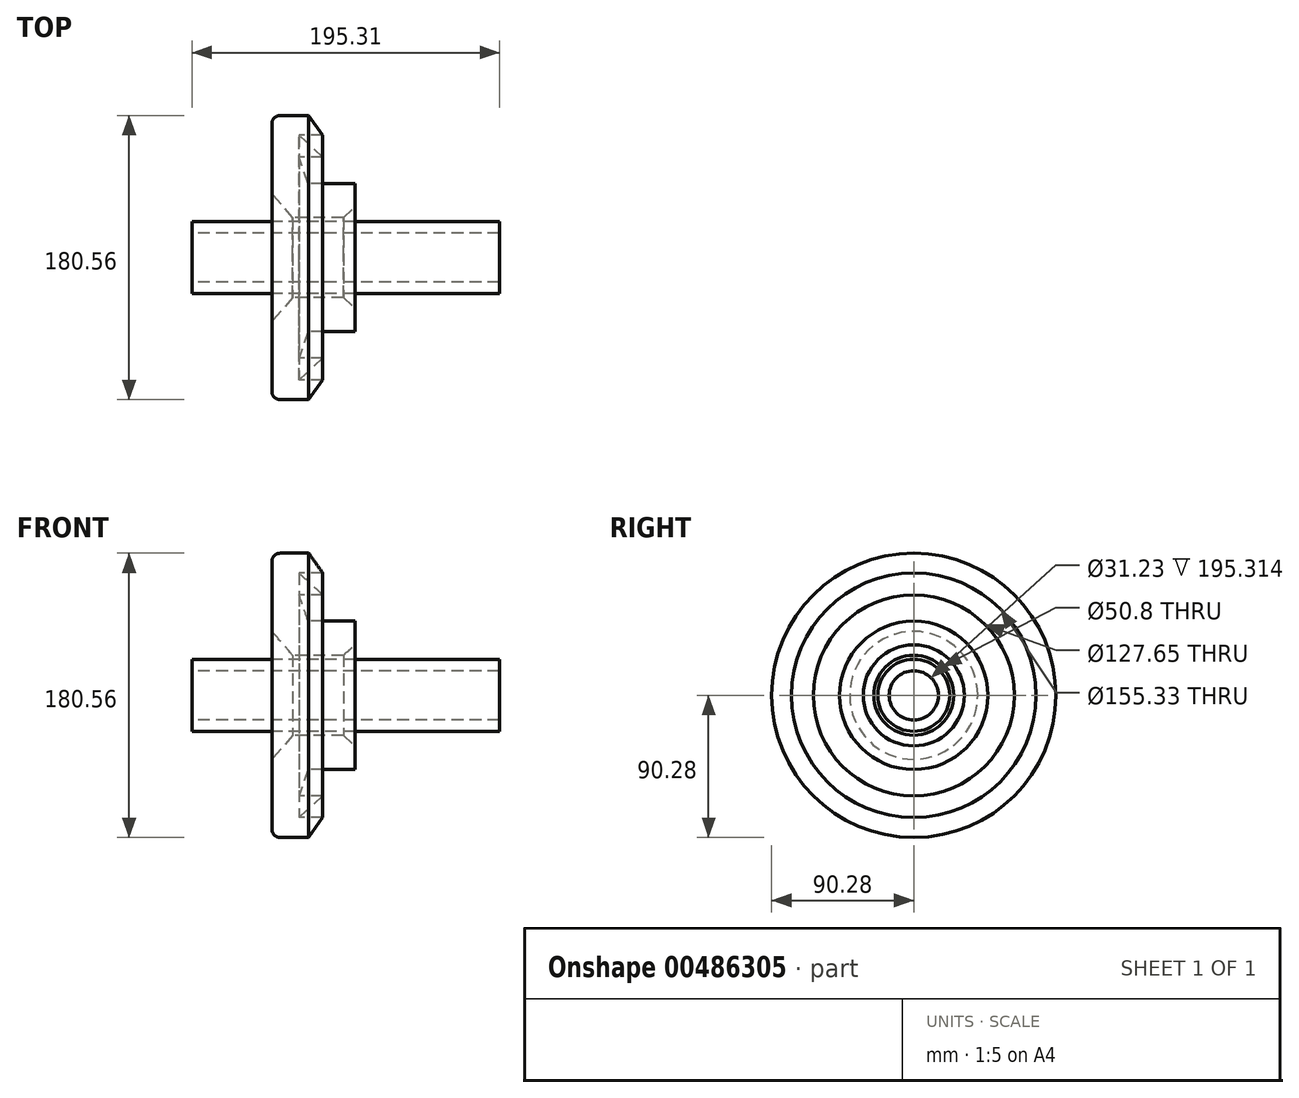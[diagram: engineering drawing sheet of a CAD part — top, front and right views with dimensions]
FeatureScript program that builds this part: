
annotation { "Feature Type Name" : "Feature", "Feature Type Description" : "" }
export const myFeature = defineFeature(function(context is Context, id is Id, definition is map)
    precondition{}
    {
        {
            var Q0;
            Q0=qCreatedBy(makeId("Front.planeOp"),FACE);
            var sketch = newSketch(context, id + "F0", { "sketchPlane" : qUnion([Q0])});
            skLineSegment(sketch, "E0", {"start": v(13.13, 0) * mm, "end": v(0, 15.22) * mm});
            skLineSegment(sketch, "E1", {"start": v(0, 15.22) * mm, "end": v(0, 64.88) * mm});
            skLineSegment(sketch, "E2", {"start": v(0, 64.88) * mm, "end": v(23.3, 64.88) * mm});
            skLineSegment(sketch, "E3", {"start": v(23.3, 64.88) * mm, "end": v(32.26, 52.26) * mm});
            skLineSegment(sketch, "E4", {"start": v(32.26, 52.26) * mm, "end": v(17.2, 52.26) * mm});
            skLineSegment(sketch, "E5", {"start": v(17.2, 52.26) * mm, "end": v(32.26, 38.42) * mm});
            skLineSegment(sketch, "E6", {"start": v(32.26, 38.42) * mm, "end": v(17.2, 38.42) * mm});
            skLineSegment(sketch, "E7", {"start": v(17.2, 38.42) * mm, "end": v(22.9, 21.74) * mm});
            skLineSegment(sketch, "E8", {"start": v(22.9, 21.74) * mm, "end": v(52.62, 21.74) * mm});
            skLineSegment(sketch, "E9", {"start": v(52.62, 21.74) * mm, "end": v(52.62, 6.68) * mm});
            skLineSegment(sketch, "E10", {"start": v(52.62, 6.68) * mm, "end": v(45.29, 0) * mm});
            skLineSegment(sketch, "E11", {"start": v(45.29, 0) * mm, "end": v(13.13, 0) * mm});
            skLineSegment(sketch, "E12", {"start": v(-104.09, -25.4) * mm, "end": v(175.13, -25.4) * mm});
            skSolve(sketch);
        }
        {
            var Q0;
            Q0=makeQuery(id+"F0.imprint","IMPRINT",FACE,{"disambiguationData":[TD([[makeQuery(id+"F0.imprint","IMPRINT",EDGE,{"derivedFrom":sQuery(id+"F0.wireOp",EDGE,"E0")}),-1.0]])]});
            var Q1;
            Q1=sQuery(id+"F0.wireOp",EDGE,"E12");
            revolve(context, id + "F1", {"surfaceOperationType" : NewSurfaceOperationType.NEW, "entities" : qUnion([Q0]), "axis" : qUnion([Q1]), "revolveType" : RevolveType.FULL});
        }
        {
            var Q0;
            Q0=qCreatedBy(makeId("Front.planeOp"),FACE);
            var sketch = newSketch(context, id + "F2", { "sketchPlane" : qUnion([Q0])});
            skLineSegment(sketch, "E13.bottom", {"start": v(-50.8, -2.54) * mm, "end": v(144.51, -2.54) * mm});
            skLineSegment(sketch, "E13.top", {"start": v(-50.8, -9.79) * mm, "end": v(144.51, -9.79) * mm});
            skLineSegment(sketch, "E13.left", {"start": v(-50.8, -2.54) * mm, "end": v(-50.8, -9.79) * mm});
            skLineSegment(sketch, "E13.right", {"start": v(144.51, -2.54) * mm, "end": v(144.51, -9.79) * mm});
            skSolve(sketch);
        }
        {
            var Q0;
            Q0=makeQuery(id+"F2.imprint","IMPRINT",FACE,{"disambiguationData":[TD([[makeQuery(id+"F2.imprint","IMPRINT",EDGE,{"derivedFrom":sQuery(id+"F2.wireOp",EDGE,"E13.bottom")}),-1.0]])]});
            var Q1;
            Q1=sQuery(id+"F0.wireOp",EDGE,"E12");
            revolve(context, id + "F3", {"surfaceOperationType" : NewSurfaceOperationType.NEW, "entities" : qUnion([Q0]), "axis" : qUnion([Q1]), "revolveType" : RevolveType.FULL});
        }
        {
            var Q0;
            Q0=makeQuery(id+"F1.opRevolve","SWEPT_EDGE",EDGE,{"disambiguationData":[OSD([sQuery(id+"F0.wireOp",EDGE,"E1"),sQuery(id+"F0.wireOp",EDGE,"E2")])]});
            fillet(context, id + "F4", {"entities" : qUnion([Q0]), "tangentPropagation" : true, "radius" : 5.08 * mm, "defaultsChanged" : false, "vertexSettings" : [], "allowEdgeOverflow" : false});
        }
    });
